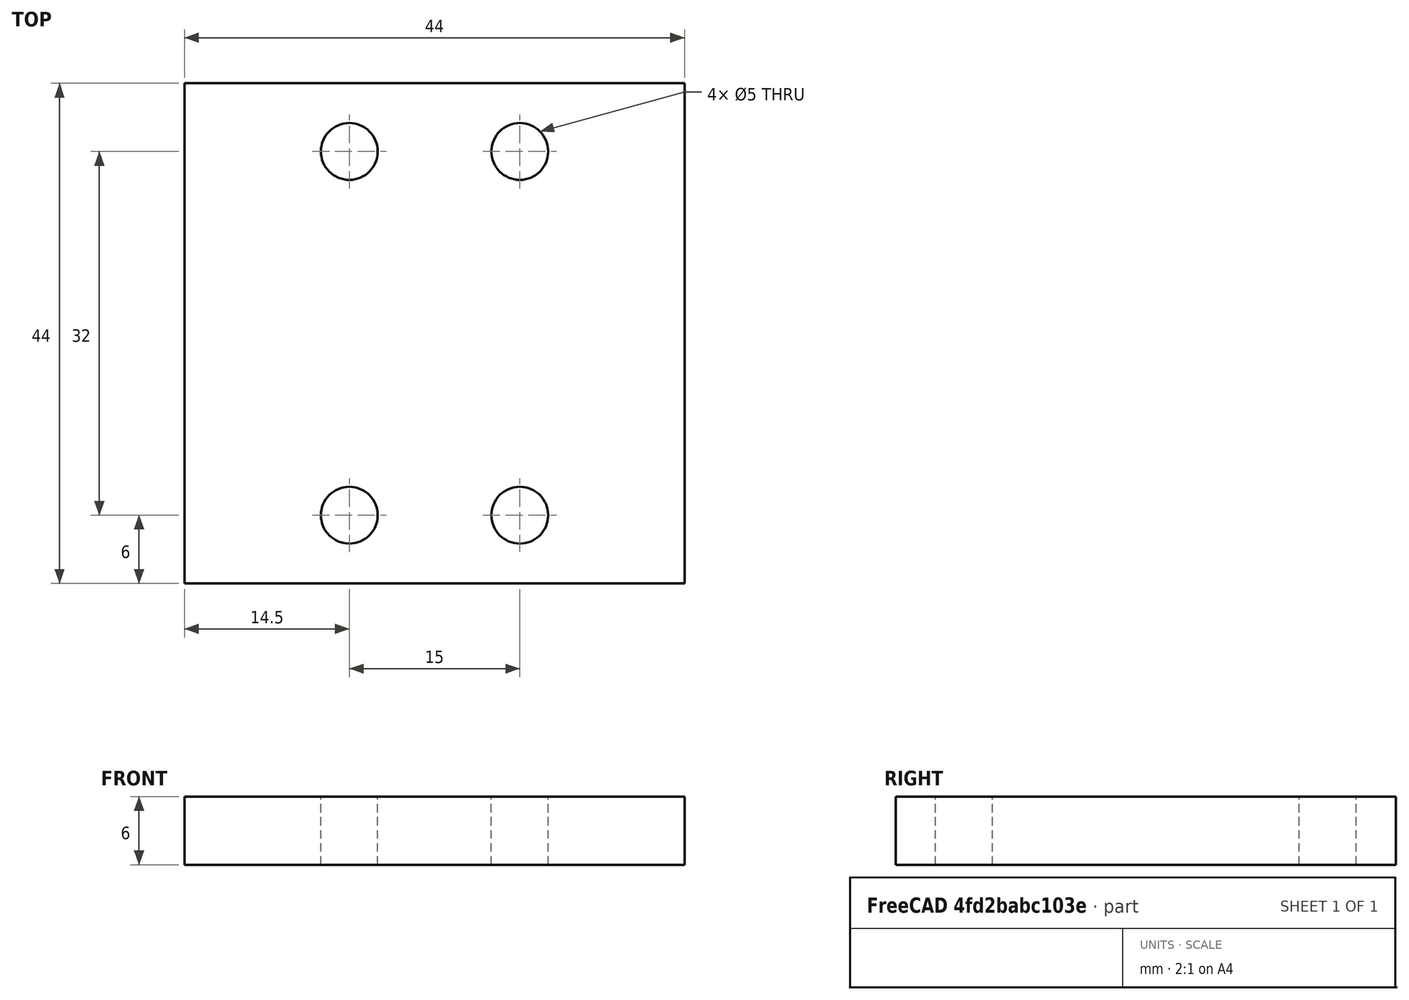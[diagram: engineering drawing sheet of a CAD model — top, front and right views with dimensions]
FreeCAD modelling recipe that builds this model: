
FCSTD DOCUMENT  (FreeCAD 0.16R)
Label: 4holes4
License: All rights reserved
LicenseURL: http://en.wikipedia.org/wiki/All_rights_reserved
objects: Part::Cylinder×4, Part::Cut×4, Part::Box×1
note: 9 computed .brp shape members not serialized (recipe doc carries the construction recipe); baked Part::Feature solids carry a one-line shape summary decoded from their .brp

FEATURE [Part::Box] Box  label="Cube"
  Height = 6
  Length = 44
  Width = 44
FEATURE [Part::Cylinder] Cylinder
  Angle = 360
  Height = 10
  Placement = pos=(14.5,6,0) rot=(0,0,1;0rad)
  Radius = 2.5
FEATURE [Part::Cylinder] Cylinder001
  Angle = 360
  Height = 10
  Placement = pos=(29.5,6,0) rot=(0,0,1;0rad)
  Radius = 2.5
FEATURE [Part::Cylinder] Cylinder002
  Angle = 360
  Height = 10
  Placement = pos=(14.5,38,0) rot=(0,0,1;0rad)
  Radius = 2.5
FEATURE [Part::Cylinder] Cylinder003
  Angle = 360
  Height = 10
  Placement = pos=(29.5,38,0) rot=(0,0,1;0rad)
  Radius = 2.5
FEATURE [Part::Cut] Cut
  Base = -> Box
  Tool = -> Cylinder
FEATURE [Part::Cut] Cut001
  Base = -> Cut
  Tool = -> Cylinder001
FEATURE [Part::Cut] Cut002
  Base = -> Cut001
  Tool = -> Cylinder003
FEATURE [Part::Cut] Cut003
  Base = -> Cut002
  Tool = -> Cylinder002
